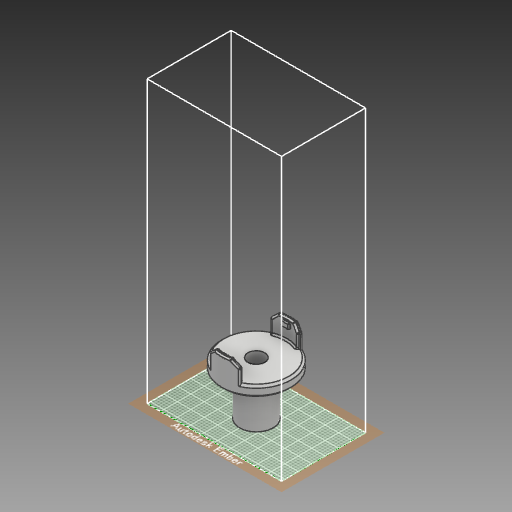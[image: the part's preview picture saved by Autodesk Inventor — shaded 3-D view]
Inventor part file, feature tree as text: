
AUTODESK INVENTOR PART (.ipt)
format: ipt  version: 2018 (Build 220112000, 112)  size: 5,263,872 bytes
history: native  units: mm
features: extrude x15, sketch x15, other x9, mirror x3, pattern_circular x3, fillet x3, projected_geometry x3, chamfer x2
ambient origin geometry x8: Origin, YZ Plane, XZ Plane, XY Plane, X Axis, Y Axis, Z Axis, Center Point
bodies: Body1 (feature_tree)
feature tree (53):
  other  "gear.ipt"
  other  "ソリッド1"
  extrude  "押し出し1"  Depth=33.0mm
  extrude  "押し出し2"  Depth=20.0mm TaperAngle=0.0deg
  mirror  "ミラー1"
  extrude  "押し出し3"  Depth=2.0mm
  mirror  "ミラー2"
  extrude  "押し出し4"  Depth=14.5mm
  mirror  "ミラー3"
  other  "結合1"
  extrude  "押し出し5"  Depth=9.2mm TaperAngle=0.0deg
  extrude  "押し出し6"  Depth=7.5mm
  pattern_circular  "円形状パターン1"  [2 undecoded]
  fillet  "フィレット1"  Radius=9.2mm
  fillet  "フィレット2"  Radius=2.5mm
  extrude  "押し出し7"  Depth=1.0mm
  chamfer  "面取り2"  Distance=1.0mm
  extrude  "押し出し8"  Depth=4.0mm TaperAngle=0.0deg
  extrude  "押し出し9"  Depth=10.0mm
  extrude  "押し出し10"  Depth=4.0mm TaperAngle=0.0deg
  extrude  "押し出し11"  TaperAngle=45.0deg  [1 undecoded]
  fillet  "フィレット3"  Radius=0.2mm
  extrude  "押し出し12"  Depth=0.2mm
  chamfer  "面取り3"  Angle=45.0deg  [1 undecoded]
  pattern_circular  "円形状パターン2"  [2 undecoded]
  extrude  "押し出し13"  Depth=220.0mm TaperAngle=360.0deg
  pattern_circular  "円形状パターン3"  [2 undecoded]
  extrude  "押し出し14"  Depth=0.5mm
  extrude  "押し出し15"  Depth=16.0mm
  sketch  "スケッチ1"
  sketch  "スケッチ2"
  sketch  "スケッチ3"
  sketch  "スケッチ4"
  other  "ソリッド1::gear.ipt"
  other  "TaggingFeature1"
  sketch  "スケッチ6"
  projected_geometry  "投影ループ1"
  sketch  "スケッチ7"
  projected_geometry  "投影ループ2"
  sketch  "スケッチ8"
  sketch  "スケッチ9"
  sketch  "スケッチ10"
  projected_geometry  "投影ループ3"
  sketch  "スケッチ12"
  sketch  "スケッチ14"
  sketch  "スケッチ15"
  sketch  "スケッチ16"
  sketch  "スケッチ17"
  sketch  "スケッチ18"
  other  "ソリッド2"
  other  "断面エッジを投影1"
  other  "断面エッジを投影2"
  other  "断面エッジを投影3"
note: 8 required parameter values undecoded (feature->parameter linkage not recoverable at this tier; creation-order binding heuristic only, values carry confidence <= 0.55)
